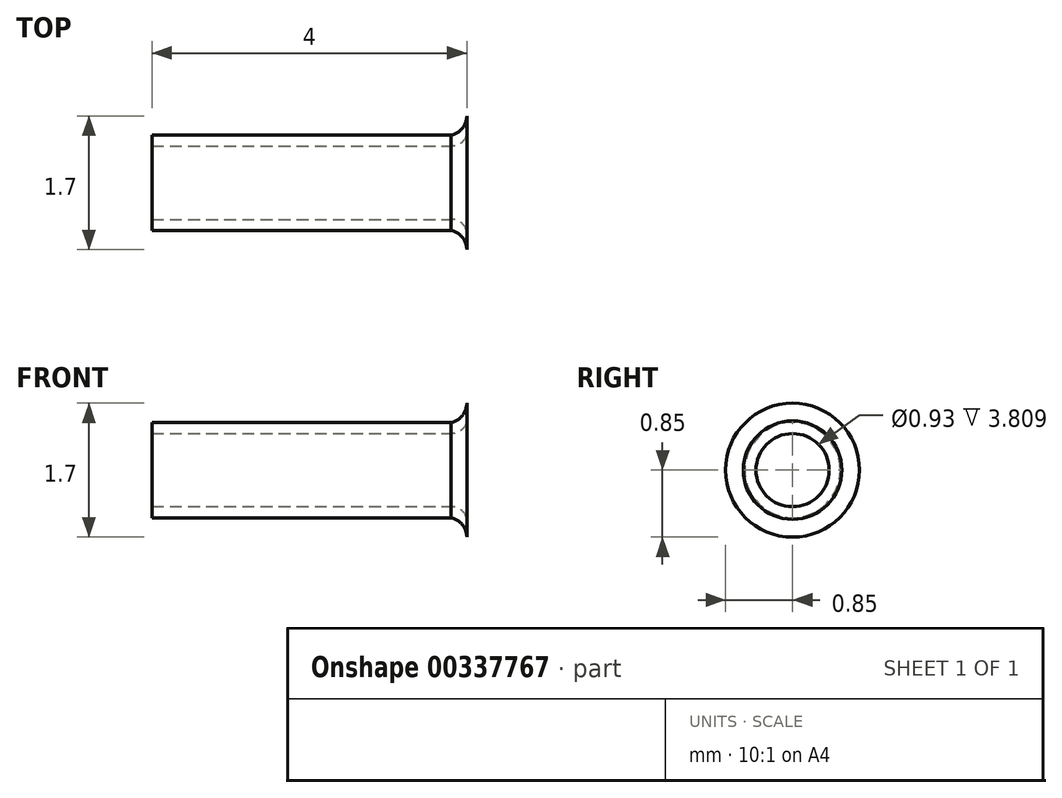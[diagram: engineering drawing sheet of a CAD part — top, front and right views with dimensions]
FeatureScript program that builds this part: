
annotation { "Feature Type Name" : "Feature", "Feature Type Description" : "" }
export const myFeature = defineFeature(function(context is Context, id is Id, definition is map)
    precondition{}
    {
        {
            var Q0;
            Q0=qCreatedBy(makeId("Top.planeOp"),FACE);
            var sketch = newSketch(context, id + "F0", { "sketchPlane" : qUnion([Q0])});
            skLineSegment(sketch, "E0", {"start": v(0, 0) * mm, "end": v(-4, 0) * mm});
            skLineSegment(sketch, "E1", {"start": v(-4, 0) * mm, "end": v(-4, 0.6) * mm});
            skLineSegment(sketch, "E2", {"start": v(-4, 0.6) * mm, "end": v(-0.2, 0.6) * mm});
            skLineSegment(sketch, "E3", {"start": v(0, 0) * mm, "end": v(0, 0.85) * mm});
            skArc(sketch, "E4", {"start": v(-0.2, 0.6) * mm, "mid": v(-0.06, 0.7) * mm, "end": v(0, 0.85) * mm});
            skLineSegment(sketch, "E5", {"start": v(-4, 0.46) * mm, "end": v(-0.2, 0.46) * mm});
            skArc(sketch, "E6", {"start": v(-0.2, 0.46) * mm, "mid": v(-0.07, 0.51) * mm, "end": v(0, 0.63) * mm});
            skSolve(sketch);
        }
        {
            var Q0;
            {var subQ3=sQuery(id+"F0.wireOp",EDGE,"E2");Q0=makeQuery(id+"F0.imprint","IMPRINT",FACE,{"disambiguationData":[TD([[makeQuery(id+"F0.imprint","IMPRINT",EDGE,{"derivedFrom":subQ3}),-1.0]])]});}
            var Q1;
            Q1=sQuery(id+"F0.wireOp",EDGE,"E0");
            revolve(context, id + "F1", {"entities" : qUnion([Q0]), "axis" : qUnion([Q1]), "revolveType" : RevolveType.FULL});
        }
    });
